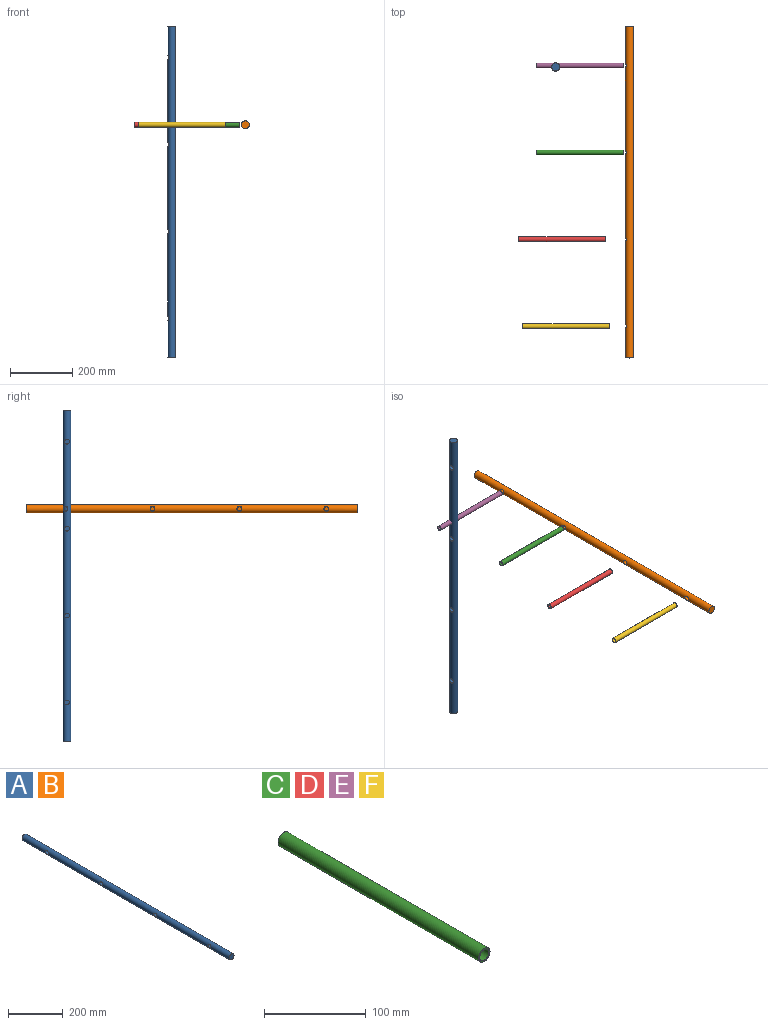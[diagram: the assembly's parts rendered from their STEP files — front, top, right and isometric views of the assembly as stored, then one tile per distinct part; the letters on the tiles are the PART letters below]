
ASSEMBLY  parts=6 mates=4
PART A: 11 faces, bbox 25.4x1066.8x25.4 mm
  f0: cylinder r=12.7mm len=1066.8mm, axis (0,1,0), area 84288.2mm2, adj f1,f2,f3,f5,f7,f9
  f1: plane 25.4x25.4mm, normal (0,-1,0), area 506.7mm2, adj f0
  f2: plane 25.4x25.4mm, normal (0,1,0), area 506.7mm2, adj f0
  f3: cylinder r=7.94mm len=15.88mm, axis (1,0,0), area 566.1mm2, adj f0,f4
  f4: plane 15.88x15.88mm, normal (-1,0,0), area 197.9mm2, adj f3
  f5: cylinder r=7.94mm len=15.88mm, axis (1,0,0), area 566.1mm2, adj f0,f6
  f6: plane 15.88x15.88mm, normal (-1,0,0), area 197.9mm2, adj f5
  f7: cylinder r=7.94mm len=15.88mm, axis (1,0,0), area 566.1mm2, adj f0,f8
  f8: plane 15.88x15.88mm, normal (-1,0,0), area 197.9mm2, adj f7
  f9: cylinder r=7.94mm len=15.88mm, axis (1,0,0), area 566.1mm2, adj f0,f10
  f10: plane 15.88x15.88mm, normal (-1,0,0), area 197.9mm2, adj f9
PART B: same geometry as A
PART C: 4 faces, bbox 15.9x279.4x15.9 mm
  f0: cylinder r=6.41mm len=279.4mm, axis (0,1,0), area 11259mm2, adj f2,f3
  f1: cylinder r=7.94mm len=279.4mm, axis (0,1,0), area 13934.5mm2, adj f2,f3
  f2: plane 15.88x15.88mm, normal (0,-1,0), area 68.7mm2, adj f0,f1
  f3: plane 15.88x15.88mm, normal (0,1,0), area 68.7mm2, adj f0,f1
PART D: same geometry as C
PART E: same geometry as C
PART F: same geometry as C
PLACE A rot(axis=(-1,0,0),90deg) t=(-136.82,-94.9,-788.71)mm
PLACE B t=(100.18,36.9,-39.51)mm fixed
PLACE C rot(axis=(-0.09,-0.09,-0.99),90.5deg) t=(82.37,-369.5,-39.51)mm
PLACE D rot(axis=(0.58,0.58,-0.58),120deg) t=(23.99,-648.9,-39.51)mm
PLACE E rot(axis=(0.58,0.58,-0.58),120deg) t=(81.57,-90.1,-39.51)mm
PLACE F rot(axis=(0.58,0.58,-0.58),120deg) t=(36.78,-928.3,-39.51)mm
MATE cylindrical F.f0 <-> B.f7  axis (1,0,0) through (36.78,-928.3,-39.51)mm
MATE cylindrical D.f0 <-> B.f5  axis (1,0,0) through (23.99,-648.9,-39.51)mm
MATE cylindrical B.f9 <-> E.f0  axis (1,0,0) through (93.78,-90.1,-39.51)mm
MATE cylindrical C.f0 <-> B.f3  axis (1,0,0) through (82.37,-369.5,-39.51)mm
